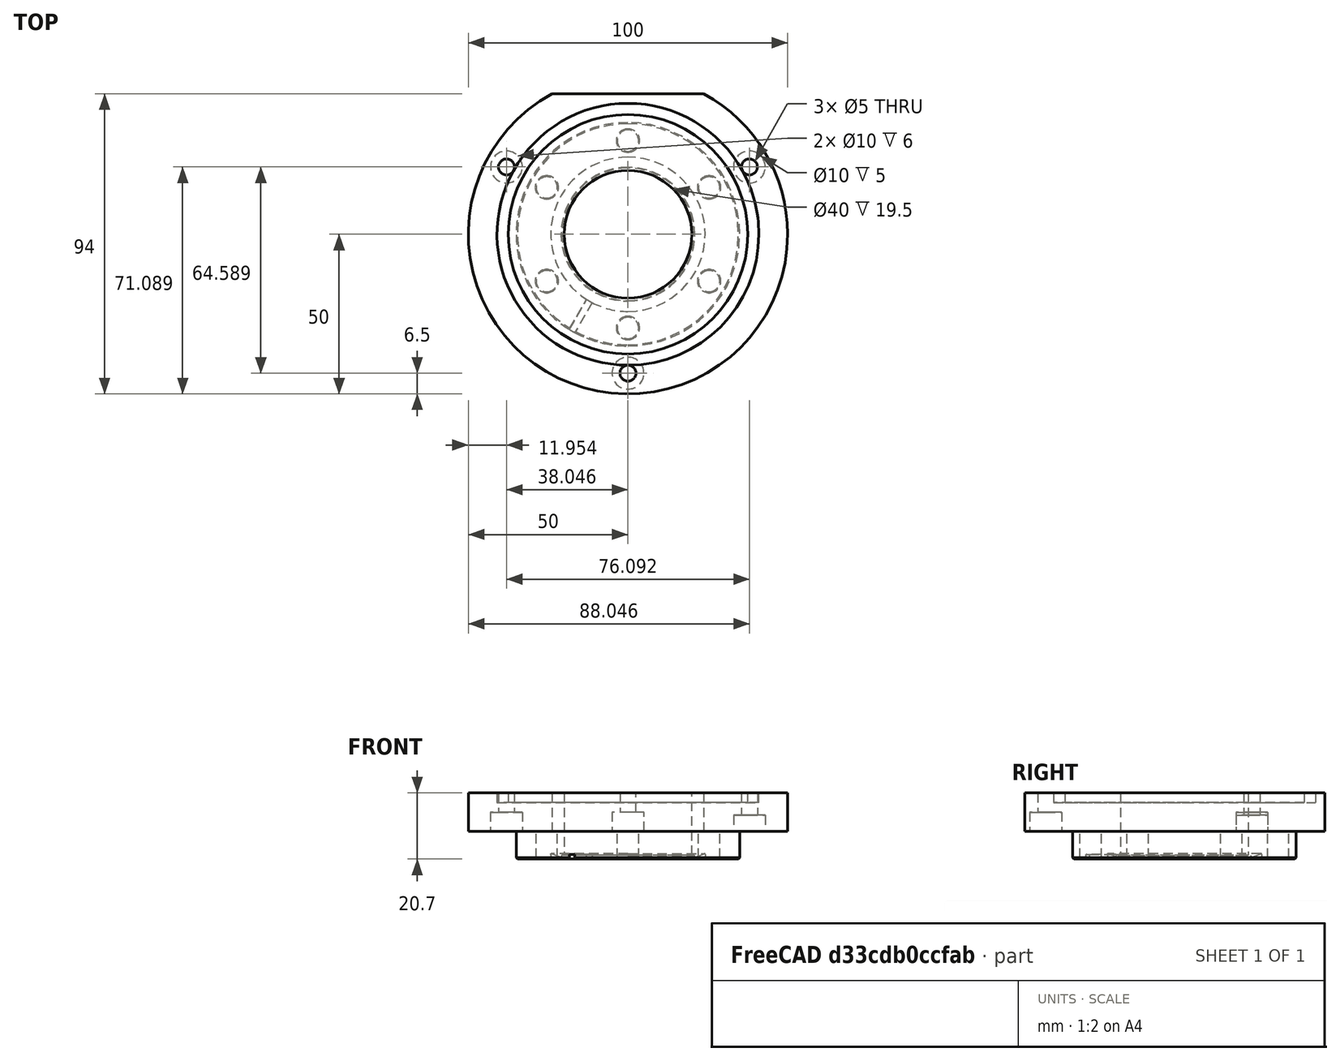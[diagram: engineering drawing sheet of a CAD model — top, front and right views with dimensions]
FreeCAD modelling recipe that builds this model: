
FCSTD DOCUMENT  (FreeCAD 0.20R)
Label: PhilipsXL30_Flange_100_TopLeft_ToCF35_CF40_ZeroLengthAdapter
License: All rights reserved
LicenseURL: http://en.wikipedia.org/wiki/All_rights_reserved
objects: TechDraw::DrawViewDimension×33, TechDraw::DrawProjGroupItem×3, TechDraw::DrawSVGTemplate×2, TechDraw::DrawPage×2, App::Link×1, Part::Feature×1, Part::Cylinder×1, Part::MultiFuse×1, Part::Cut×1, TechDraw::DrawProjGroup×1, TechDraw::DrawViewPart×1, TechDraw::DrawViewSection×1
note: 4 computed .brp shape members not serialized (recipe doc carries the construction recipe); baked Part::Feature solids carry a one-line shape summary decoded from their .brp
EXTERNAL_REF file=PhilipsXL30_Blindflange_100_TopBack.FCStd obj=Cut004

FEATURE [App::Link] Link  label="XL30TopBackFlange100"
  LinkedObject = -> <external PhilipsXL30_Blindflange_100_TopBack.FCStd>#Cut004
FEATURE [Part::Feature] Solid  label="CF35 Flange"
  Placement = pos=(0,0,4) rot=(1,0,0;-1.5708rad)
  shape: bbox 70 x 70 x 12.7 mm, 58 faces (baked)
FEATURE [Part::Cylinder] Cylinder
  Angle = 360
  AttacherType = Attacher::AttachEngine3D
  FirstAngle = 0
  Height = 30
  Placement = pos=(0,0,-10) rot=(0,0,1;0rad)
  Radius = 20
  SecondAngle = 0
FEATURE [Part::MultiFuse] Fusion
  Shapes = -> [Solid,Link]
FEATURE [Part::Cut] Cut  label="PhilipsXL30_Flange_100_TopLeft_ToCF35_CF40"
  Base = -> Fusion
  Tool = -> Cylinder
FEATURE [TechDraw::DrawSVGTemplate] Template
  EditableTexts = Designed_by_Name=Thomas Spielauer; FC-Date=2023-12-18; FC-SC=mm; FC-SH=1/1; FC-Title=XL30 top 100mm flange; Subtitle=CF35/CF40 adapter
  Height = 210
  Orientation = 1
  Width = 297
FEATURE [TechDraw::DrawProjGroupItem] ProjItem  label="Front"
  CoarseView = false
  Direction = (0,0,-1)
  Focus = 100
  HardHidden = false
  IsoCount = 0
  IsoHidden = false
  IsoVisible = false
  LockPosition = true
  Perspective = false
  Rotation = 0
  RotationVector = (1,0,0)
  ScaleType = 2
  SeamHidden = false
  SeamVisible = true
  SmoothHidden = false
  SmoothVisible = true
  Source = -> [Cut]
  Type = 0
  X = 0
  XDirection = (1,0,0)
  Y = 0
FEATURE [TechDraw::DrawProjGroupItem] ProjItem001  label="Rear"
  CoarseView = false
  Direction = (0,0,1)
  Focus = 100
  HardHidden = false
  IsoCount = 0
  IsoHidden = false
  IsoVisible = false
  LockPosition = false
  Perspective = false
  Rotation = 0
  RotationVector = (1,0,0)
  ScaleType = 2
  SeamHidden = false
  SeamVisible = true
  SmoothHidden = false
  SmoothVisible = true
  Source = -> [Cut]
  Type = 3
  X = 127.958
  XDirection = (-1,0,0)
  Y = 0
FEATURE [TechDraw::DrawProjGroupItem] ProjItem002  label="Top"
  CoarseView = false
  Direction = (0,-1,0)
  Focus = 100
  HardHidden = false
  IsoCount = 0
  IsoHidden = false
  IsoVisible = false
  LockPosition = false
  Perspective = false
  Rotation = 0
  RotationVector = (1,0,0)
  ScaleType = 2
  SeamHidden = false
  SeamVisible = true
  SmoothHidden = false
  SmoothVisible = true
  Source = -> [Cut]
  Type = 4
  X = 0
  XDirection = (1,0,0)
  Y = -96.0417
FEATURE [TechDraw::DrawProjGroup] ProjGroup
  Anchor = -> ProjItem
  AutoDistribute = false
  LockPosition = false
  ProjectionType = 0
  Rotation = 0
  ScaleType = 0
  Source = -> [Cut]
  Views = -> [ProjItem,ProjItem001,ProjItem002]
  X = 79.1352
  Y = 132.441
  spacingX = 15
  spacingY = 15
FEATURE [TechDraw::DrawViewDimension] Dimension
  AngleOverride = false
  Arbitrary = false
  ArbitraryTolerances = false
  EqualTolerance = true
  ExtensionAngle = 0
  FormatSpec = %.2w
  FormatSpecOverTolerance = %+.2w
  FormatSpecUnderTolerance = %+.2w
  Inverted = false
  LineAngle = 0
  LockPosition = false
  MeasureType = 1
  OverTolerance = 0
  References2D = -> [ProjItem002]
  Rotation = 0
  ScaleType = 0
  TheoreticalExact = false
  Type = 0
  UnderTolerance = 0
  X = 2.17883
  Y = 22.0034
FEATURE [TechDraw::DrawViewDimension] Dimension001
  AngleOverride = false
  Arbitrary = false
  ArbitraryTolerances = false
  EqualTolerance = true
  ExtensionAngle = 0
  FormatSpec = %.2w
  FormatSpecOverTolerance = %+.2w
  FormatSpecUnderTolerance = %+.2w
  Inverted = false
  LineAngle = 0
  LockPosition = false
  MeasureType = 1
  OverTolerance = 0
  References2D = -> [ProjItem002]
  Rotation = 0
  ScaleType = 0
  TheoreticalExact = false
  Type = 0
  UnderTolerance = 0
  X = 27.4411
  Y = -14.8634
FEATURE [TechDraw::DrawViewDimension] Dimension002
  AngleOverride = false
  Arbitrary = false
  ArbitraryTolerances = false
  EqualTolerance = true
  ExtensionAngle = 0
  FormatSpec = %.2w
  FormatSpecOverTolerance = %+.2w
  FormatSpecUnderTolerance = %+.2w
  Inverted = false
  LineAngle = 0
  LockPosition = false
  MeasureType = 1
  OverTolerance = 0
  References2D = -> [ProjItem002]
  Rotation = 0
  ScaleType = 0
  TheoreticalExact = false
  Type = 0
  UnderTolerance = 0
  X = 54.1502
  Y = 18.5378
FEATURE [TechDraw::DrawViewDimension] Dimension003
  AngleOverride = false
  Arbitrary = false
  ArbitraryTolerances = false
  EqualTolerance = true
  ExtensionAngle = 0
  FormatSpec = %.2w
  FormatSpecOverTolerance = %+.2w
  FormatSpecUnderTolerance = %+.2w
  Inverted = false
  LineAngle = 0
  LockPosition = false
  MeasureType = 1
  OverTolerance = 0
  References2D = -> [ProjItem002]
  Rotation = 0
  ScaleType = 0
  TheoreticalExact = false
  Type = 0
  UnderTolerance = 0
  X = 63.3782
  Y = -2.04705
FEATURE [TechDraw::DrawViewDimension] Dimension004
  AngleOverride = false
  Arbitrary = false
  ArbitraryTolerances = false
  EqualTolerance = true
  ExtensionAngle = 0
  FormatSpec = ⌀%.2w
  FormatSpecOverTolerance = %+.2w
  FormatSpecUnderTolerance = %+.2w
  Inverted = false
  LineAngle = 0
  LockPosition = false
  MeasureType = 1
  OverTolerance = 0
  References2D = -> [ProjItem]
  Rotation = 0
  ScaleType = 0
  TheoreticalExact = false
  Type = 5
  UnderTolerance = 0
  X = 57.5648
  Y = 13.2744
FEATURE [TechDraw::DrawViewDimension] Dimension005
  AngleOverride = false
  Arbitrary = false
  ArbitraryTolerances = false
  EqualTolerance = true
  ExtensionAngle = 0
  FormatSpec = ⌀%.2w
  FormatSpecOverTolerance = %+.2w
  FormatSpecUnderTolerance = %+.2w
  Inverted = false
  LineAngle = 0
  LockPosition = false
  MeasureType = 1
  OverTolerance = 0
  References2D = -> [ProjItem]
  Rotation = 0
  ScaleType = 0
  TheoreticalExact = false
  Type = 5
  UnderTolerance = 0
  X = 57.82
  Y = 6.25427
FEATURE [TechDraw::DrawViewDimension] Dimension006
  AngleOverride = false
  Arbitrary = false
  ArbitraryTolerances = false
  EqualTolerance = true
  ExtensionAngle = 0
  FormatSpec = ⌀%.2w
  FormatSpecOverTolerance = %+.2w
  FormatSpecUnderTolerance = %+.2w
  Inverted = false
  LineAngle = 0
  LockPosition = false
  MeasureType = 1
  OverTolerance = 0
  References2D = -> [ProjItem]
  Rotation = 0
  ScaleType = 0
  TheoreticalExact = false
  Type = 5
  UnderTolerance = 0
  X = 57.9477
  Y = 0.127638
FEATURE [TechDraw::DrawViewDimension] Dimension007
  AngleOverride = false
  Arbitrary = false
  ArbitraryTolerances = false
  EqualTolerance = true
  ExtensionAngle = 0
  FormatSpec = ⌀%.2w
  FormatSpecOverTolerance = %+.2w
  FormatSpecUnderTolerance = %+.2w
  Inverted = false
  LineAngle = 0
  LockPosition = false
  MeasureType = 1
  OverTolerance = 0
  References2D = -> [ProjItem]
  Rotation = 0
  ScaleType = 0
  TheoreticalExact = false
  Type = 5
  UnderTolerance = 0
  X = 59.0326
  Y = -6.3819
FEATURE [TechDraw::DrawViewDimension] Dimension008
  AngleOverride = false
  Arbitrary = false
  ArbitraryTolerances = false
  EqualTolerance = true
  ExtensionAngle = 0
  FormatSpec = %.2w
  FormatSpecOverTolerance = %+.2w
  FormatSpecUnderTolerance = %+.2w
  Inverted = false
  LineAngle = 0
  LockPosition = false
  MeasureType = 1
  OverTolerance = 0
  References2D = -> [ProjItem]
  Rotation = 0
  ScaleType = 0
  TheoreticalExact = false
  Type = 6
  UnderTolerance = 0
  X = -7.97738
  Y = 12.9765
FEATURE [TechDraw::DrawViewDimension] Dimension009
  AngleOverride = false
  Arbitrary = false
  ArbitraryTolerances = false
  EqualTolerance = true
  ExtensionAngle = 0
  FormatSpec = ⌀%.2w (6x M6 tapped)
  FormatSpecOverTolerance = %+.2w
  FormatSpecUnderTolerance = %+.2w
  Inverted = false
  LineAngle = 0
  LockPosition = false
  MeasureType = 1
  OverTolerance = 0
  References2D = -> [ProjItem]
  Rotation = 0
  ScaleType = 0
  TheoreticalExact = false
  Type = 5
  UnderTolerance = 0
  X = 67.2397
  Y = 38.5978
FEATURE [TechDraw::DrawViewDimension] Dimension010
  AngleOverride = false
  Arbitrary = false
  ArbitraryTolerances = false
  EqualTolerance = true
  ExtensionAngle = 0
  FormatSpec = %.2w
  FormatSpecOverTolerance = %+.2w
  FormatSpecUnderTolerance = %+.2w
  Inverted = false
  LineAngle = 0
  LockPosition = false
  MeasureType = 1
  OverTolerance = 0
  References2D = -> [ProjItem]
  Rotation = 0
  ScaleType = 0
  TheoreticalExact = false
  Type = 6
  UnderTolerance = 0
  X = -38.6576
  Y = -43.0065
FEATURE [TechDraw::DrawViewDimension] Dimension011
  AngleOverride = false
  Arbitrary = false
  ArbitraryTolerances = false
  EqualTolerance = true
  ExtensionAngle = 0
  FormatSpec = %.2w
  FormatSpecOverTolerance = %+.2w
  FormatSpecUnderTolerance = %+.2w
  Inverted = false
  LineAngle = 0
  LockPosition = false
  MeasureType = 1
  OverTolerance = 0
  References2D = -> [ProjItem]
  Rotation = 0
  ScaleType = 0
  TheoreticalExact = false
  Type = 6
  UnderTolerance = 0
  X = 36.9663
  Y = -44.9394
FEATURE [TechDraw::DrawViewDimension] Dimension012
  AngleOverride = false
  Arbitrary = false
  ArbitraryTolerances = false
  EqualTolerance = true
  ExtensionAngle = 0
  FormatSpec = ⌀%.2w (3x)
  FormatSpecOverTolerance = %+.2w
  FormatSpecUnderTolerance = %+.2w
  Inverted = false
  LineAngle = 0
  LockPosition = false
  MeasureType = 1
  OverTolerance = 0
  References2D = -> [ProjItem]
  Rotation = 0
  ScaleType = 0
  TheoreticalExact = false
  Type = 5
  UnderTolerance = 0
  X = 30.2012
  Y = 53.3555
FEATURE [TechDraw::DrawViewDimension] Dimension013
  AngleOverride = false
  Arbitrary = false
  ArbitraryTolerances = false
  EqualTolerance = true
  ExtensionAngle = 0
  FormatSpec = ⌀%.2w (3x)
  FormatSpecOverTolerance = %+.2w
  FormatSpecUnderTolerance = %+.2w
  Inverted = false
  LineAngle = 0
  LockPosition = false
  MeasureType = 1
  OverTolerance = 0
  References2D = -> [ProjItem]
  Rotation = 0
  ScaleType = 0
  TheoreticalExact = false
  Type = 5
  UnderTolerance = 0
  X = 26.6777
  Y = 60.4025
FEATURE [TechDraw::DrawViewDimension] Dimension014
  AngleOverride = false
  Arbitrary = false
  ArbitraryTolerances = false
  EqualTolerance = true
  ExtensionAngle = 0
  FormatSpec = ⌀%.2w
  FormatSpecOverTolerance = %+.2w
  FormatSpecUnderTolerance = %+.2w
  Inverted = false
  LineAngle = 0
  LockPosition = false
  MeasureType = 1
  OverTolerance = 0
  References2D = -> [ProjItem]
  Rotation = 0
  ScaleType = 0
  TheoreticalExact = false
  Type = 5
  UnderTolerance = 0
  X = -38.5978
  Y = 39.2594
FEATURE [TechDraw::DrawViewDimension] Dimension015
  AngleOverride = false
  Arbitrary = false
  ArbitraryTolerances = false
  EqualTolerance = true
  ExtensionAngle = 0
  FormatSpec = ⌀%.2w
  FormatSpecOverTolerance = %+.2w
  FormatSpecUnderTolerance = %+.2w
  Inverted = false
  LineAngle = 0
  LockPosition = false
  MeasureType = 1
  OverTolerance = 0
  References2D = -> [ProjItem]
  Rotation = 0
  ScaleType = 0
  TheoreticalExact = false
  Type = 5
  UnderTolerance = 0
  X = -46.979
  Y = 34.6277
FEATURE [TechDraw::DrawViewDimension] Dimension016
  AngleOverride = false
  Arbitrary = false
  ArbitraryTolerances = false
  EqualTolerance = true
  ExtensionAngle = 0
  FormatSpec = ⌀%.2w
  FormatSpecOverTolerance = %+.2w
  FormatSpecUnderTolerance = %+.2w
  Inverted = false
  LineAngle = 0
  LockPosition = false
  MeasureType = 1
  OverTolerance = 0
  References2D = -> [ProjItem001]
  Rotation = 0
  ScaleType = 0
  TheoreticalExact = false
  Type = 5
  UnderTolerance = 0
  X = 10.3892
  Y = 2.17449
FEATURE [TechDraw::DrawViewDimension] Dimension017
  AngleOverride = false
  Arbitrary = false
  ArbitraryTolerances = false
  EqualTolerance = true
  ExtensionAngle = 0
  FormatSpec = ⌀%.2w
  FormatSpecOverTolerance = %+.2w
  FormatSpecUnderTolerance = %+.2w
  Inverted = false
  LineAngle = 0
  LockPosition = false
  MeasureType = 1
  OverTolerance = 0
  References2D = -> [ProjItem001]
  Rotation = 0
  ScaleType = 0
  TheoreticalExact = false
  Type = 5
  UnderTolerance = 0
  X = 61.8521
  Y = -7.24829
FEATURE [TechDraw::DrawViewDimension] Dimension018
  AngleOverride = false
  Arbitrary = false
  ArbitraryTolerances = false
  EqualTolerance = true
  ExtensionAngle = 0
  FormatSpec = ⌀%.2w
  FormatSpecOverTolerance = %+.2w
  FormatSpecUnderTolerance = %+.2w
  Inverted = false
  LineAngle = 0
  LockPosition = false
  MeasureType = 1
  OverTolerance = 0
  References2D = -> [ProjItem001]
  Rotation = 0
  ScaleType = 0
  TheoreticalExact = false
  Type = 5
  UnderTolerance = 0
  X = 62.8321
  Y = -16.0266
FEATURE [TechDraw::DrawViewDimension] Dimension019
  AngleOverride = false
  Arbitrary = false
  ArbitraryTolerances = false
  EqualTolerance = true
  ExtensionAngle = 0
  FormatSpec = ⌀%.2w
  FormatSpecOverTolerance = %+.2w
  FormatSpecUnderTolerance = %+.2w
  Inverted = false
  LineAngle = 0
  LockPosition = false
  MeasureType = 1
  OverTolerance = 0
  References2D = -> [ProjItem001]
  Rotation = 0
  ScaleType = 0
  TheoreticalExact = false
  Type = 5
  UnderTolerance = 0
  X = 24.475
  Y = 51.9008
FEATURE [TechDraw::DrawViewDimension] Dimension020
  AngleOverride = false
  Arbitrary = false
  ArbitraryTolerances = false
  EqualTolerance = true
  ExtensionAngle = 0
  FormatSpec = %.2w
  FormatSpecOverTolerance = %+.2w
  FormatSpecUnderTolerance = %+.2w
  Inverted = false
  LineAngle = 0
  LockPosition = false
  MeasureType = 1
  OverTolerance = 0
  References2D = -> [ProjItem001]
  Rotation = 0
  ScaleType = 0
  TheoreticalExact = false
  Type = 2
  UnderTolerance = 0
  X = -48.8638
  Y = -46.6706
FEATURE [TechDraw::DrawPage] Page
  KeepUpdated = true
  NextBalloonIndex = 1
  ProjectionType = 0
  Template = -> Template
  Views = -> [ProjGroup,Dimension,Dimension001,Dimension002,Dimension003,Dimension004,Dimension005,Dimension006,Dimension007,Dimension008,Dimension009,Dimension010,Dimension011,Dimension012,Dimension013,Dimension014,Dimension015,Dimension016,Dimension017,Dimension018,Dimension019,Dimension020]
FEATURE [TechDraw::DrawSVGTemplate] Template001
  EditableTexts = Designed_by_Name=Thomas Spielauer; FC-Date=2023-12-18; FC-SC=mm; FC-SH=2/2; FC-Title=XL30 top 100mm flange; Subtitle=CF35/CF40 adapter
  Height = 210
  Orientation = 1
  Width = 297
FEATURE [TechDraw::DrawViewPart] View
  CoarseView = false
  Direction = (0,0,-1)
  Focus = 100
  HardHidden = false
  IsoCount = 0
  IsoHidden = false
  IsoVisible = false
  LockPosition = false
  Perspective = false
  Rotation = 0
  ScaleType = 0
  SeamHidden = false
  SeamVisible = true
  SmoothHidden = false
  SmoothVisible = true
  Source = -> [Cut]
  X = 89.0445
  XDirection = (1,0,0)
  Y = 130.917
FEATURE [TechDraw::DrawViewSection] SectionView  label="Section  - "
  BaseView = -> View
  CoarseView = false
  CutSurfaceDisplay = 2
  Direction = (-1,0,0)
  FileGeomPattern = <path>
  FileHatchPattern = <path>
  Focus = 100
  FuseBeforeCut = false
  HardHidden = false
  HatchScale = 1
  IsoCount = 0
  IsoHidden = false
  IsoVisible = false
  LockPosition = false
  NameGeomPattern = Diamond
  Perspective = false
  Rotation = 0
  ScaleType = 0
  SeamHidden = false
  SeamVisible = true
  SectionDirection = 0
  SectionNormal = (-1,0,0)
  SectionOrigin = (0.044,-2.97,1.71)
  SmoothHidden = false
  SmoothVisible = true
  Source = -> [Cut]
  X = 200.027
  XDirection = (0,0,-1)
  Y = 132.591
FEATURE [TechDraw::DrawViewDimension] Dimension021
  AngleOverride = false
  Arbitrary = false
  ArbitraryTolerances = false
  EqualTolerance = true
  ExtensionAngle = 0
  FormatSpec = %.2w
  FormatSpecOverTolerance = %+.2w
  FormatSpecUnderTolerance = %+.2w
  Inverted = false
  LineAngle = 0
  LockPosition = false
  MeasureType = 1
  OverTolerance = 0
  References2D = -> [SectionView]
  Rotation = 0
  ScaleType = 0
  TheoreticalExact = false
  Type = 0
  UnderTolerance = 0
  X = 22.4867
  Y = 62.4908
FEATURE [TechDraw::DrawViewDimension] Dimension022
  AngleOverride = false
  Arbitrary = false
  ArbitraryTolerances = false
  EqualTolerance = true
  ExtensionAngle = 0
  FormatSpec = %.2w
  FormatSpecOverTolerance = %+.2w
  FormatSpecUnderTolerance = %+.2w
  Inverted = false
  LineAngle = 0
  LockPosition = false
  MeasureType = 1
  OverTolerance = 0
  References2D = -> [SectionView]
  Rotation = 0
  ScaleType = 0
  TheoreticalExact = false
  Type = 0
  UnderTolerance = 0
  X = 28.4237
  Y = 57.1222
FEATURE [TechDraw::DrawViewDimension] Dimension023
  AngleOverride = false
  Arbitrary = false
  ArbitraryTolerances = false
  EqualTolerance = true
  ExtensionAngle = 0
  FormatSpec = %.2w
  FormatSpecOverTolerance = %+.2w
  FormatSpecUnderTolerance = %+.2w
  Inverted = false
  LineAngle = 0
  LockPosition = false
  MeasureType = 1
  OverTolerance = 0
  References2D = -> [SectionView]
  Rotation = 0
  ScaleType = 0
  TheoreticalExact = false
  Type = 0
  UnderTolerance = 0
  X = -17.4707
  Y = 33.3492
FEATURE [TechDraw::DrawViewDimension] Dimension024
  AngleOverride = false
  Arbitrary = false
  ArbitraryTolerances = false
  EqualTolerance = true
  ExtensionAngle = 0
  FormatSpec = %.2w
  FormatSpecOverTolerance = %+.2w
  FormatSpecUnderTolerance = %+.2w
  Inverted = false
  LineAngle = 0
  LockPosition = false
  MeasureType = 1
  OverTolerance = 0
  References2D = -> [SectionView]
  Rotation = 0
  ScaleType = 0
  TheoreticalExact = false
  Type = 0
  UnderTolerance = 0
  X = -19.1746
  Y = -50.6662
FEATURE [TechDraw::DrawViewDimension] Dimension025
  AngleOverride = false
  Arbitrary = false
  ArbitraryTolerances = false
  EqualTolerance = true
  ExtensionAngle = 0
  FormatSpec = %.2w
  FormatSpecOverTolerance = %+.2w
  FormatSpecUnderTolerance = %+.2w
  Inverted = false
  LineAngle = 0
  LockPosition = false
  MeasureType = 1
  OverTolerance = 0
  References2D = -> [SectionView]
  Rotation = 0
  ScaleType = 0
  TheoreticalExact = false
  Type = 0
  UnderTolerance = 0
  X = -22.1269
  Y = -32.6613
FEATURE [TechDraw::DrawViewDimension] Dimension026
  AngleOverride = false
  Arbitrary = false
  ArbitraryTolerances = false
  EqualTolerance = true
  ExtensionAngle = 0
  FormatSpec = %.2w (6x M6 tap)
  FormatSpecOverTolerance = %+.2w
  FormatSpecUnderTolerance = %+.2w
  Inverted = false
  LineAngle = 0
  LockPosition = false
  MeasureType = 1
  OverTolerance = 0
  References2D = -> [SectionView]
  Rotation = 0
  ScaleType = 0
  TheoreticalExact = false
  Type = 0
  UnderTolerance = 0
  X = 49.2937
  Y = -46.4369
FEATURE [TechDraw::DrawViewDimension] Dimension027
  AngleOverride = false
  Arbitrary = false
  ArbitraryTolerances = false
  EqualTolerance = true
  ExtensionAngle = 0
  FormatSpec = %.2w (CF35 knife edge)
  FormatSpecOverTolerance = %+.2w
  FormatSpecUnderTolerance = %+.2w
  Inverted = false
  LineAngle = 0
  LockPosition = false
  MeasureType = 1
  OverTolerance = 0
  References2D = -> [SectionView]
  Rotation = 0
  ScaleType = 0
  TheoreticalExact = false
  Type = 0
  UnderTolerance = 0
  X = 73.0567
  Y = 4.51126
FEATURE [TechDraw::DrawViewDimension] Dimension028
  AngleOverride = false
  Arbitrary = false
  ArbitraryTolerances = false
  EqualTolerance = true
  ExtensionAngle = 0
  FormatSpec = %.2w
  FormatSpecOverTolerance = %+.2w
  FormatSpecUnderTolerance = %+.2w
  Inverted = false
  LineAngle = 0
  LockPosition = false
  MeasureType = 1
  OverTolerance = 0
  References2D = -> [SectionView]
  Rotation = 0
  ScaleType = 0
  TheoreticalExact = false
  Type = 0
  UnderTolerance = 0
  X = 65.4609
  Y = -14.432
FEATURE [TechDraw::DrawViewDimension] Dimension029
  AngleOverride = false
  Arbitrary = false
  ArbitraryTolerances = false
  EqualTolerance = true
  ExtensionAngle = 0
  FormatSpec = %.2w
  FormatSpecOverTolerance = %+.2w
  FormatSpecUnderTolerance = %+.2w
  Inverted = false
  LineAngle = 0
  LockPosition = false
  MeasureType = 1
  OverTolerance = 0
  References2D = -> [SectionView]
  Rotation = 0
  ScaleType = 0
  TheoreticalExact = false
  Type = 0
  UnderTolerance = 0
  X = -19.9484
  Y = 2.87369
FEATURE [TechDraw::DrawViewDimension] Dimension030
  AngleOverride = false
  Arbitrary = false
  ArbitraryTolerances = false
  EqualTolerance = true
  ExtensionAngle = 0
  FormatSpec = %.2w (CF35/CF40 knife)
  FormatSpecOverTolerance = %+.2w
  FormatSpecUnderTolerance = %+.2w
  Inverted = false
  LineAngle = 0
  LockPosition = false
  MeasureType = 1
  OverTolerance = 0
  References2D = -> [SectionView]
  Rotation = 0
  ScaleType = 0
  TheoreticalExact = false
  Type = 0
  UnderTolerance = 0
  X = 37.3487
  Y = -11.5023
FEATURE [TechDraw::DrawViewDimension] Dimension031
  AngleOverride = false
  Arbitrary = false
  ArbitraryTolerances = false
  EqualTolerance = true
  ExtensionAngle = 0
  FormatSpec = %.2w (CF35/CF40)
  FormatSpecOverTolerance = %+.2w
  FormatSpecUnderTolerance = %+.2w
  Inverted = false
  LineAngle = 0
  LockPosition = false
  MeasureType = 1
  OverTolerance = 0
  References2D = -> [SectionView]
  Rotation = 0
  ScaleType = 0
  TheoreticalExact = false
  Type = 0
  UnderTolerance = 0
  X = 32.5815
  Y = -17.529
FEATURE [TechDraw::DrawViewDimension] Dimension032
  AngleOverride = false
  Arbitrary = false
  ArbitraryTolerances = false
  EqualTolerance = true
  ExtensionAngle = 0
  FormatSpec = %.2w (approx 1mm deep leak testing groove
  FormatSpecOverTolerance = %+.2w)
  FormatSpecUnderTolerance = %+.2w)
  Inverted = false
  LineAngle = 0
  LockPosition = false
  MeasureType = 1
  OverTolerance = 0
  References2D = -> [View]
  Rotation = 0
  ScaleType = 0
  TheoreticalExact = false
  Type = 0
  UnderTolerance = 0
  X = -36.6487
  Y = 49.1392
FEATURE [TechDraw::DrawPage] Page001
  KeepUpdated = true
  NextBalloonIndex = 1
  ProjectionType = 0
  Template = -> Template001
  Views = -> [View,SectionView,Dimension021,Dimension022,Dimension023,Dimension024,Dimension025,Dimension026,Dimension027,Dimension028,Dimension029,Dimension030,Dimension031,Dimension032]
note: 2 file-system paths scrubbed to <path> (originals preserved in the JSON sidecar)
